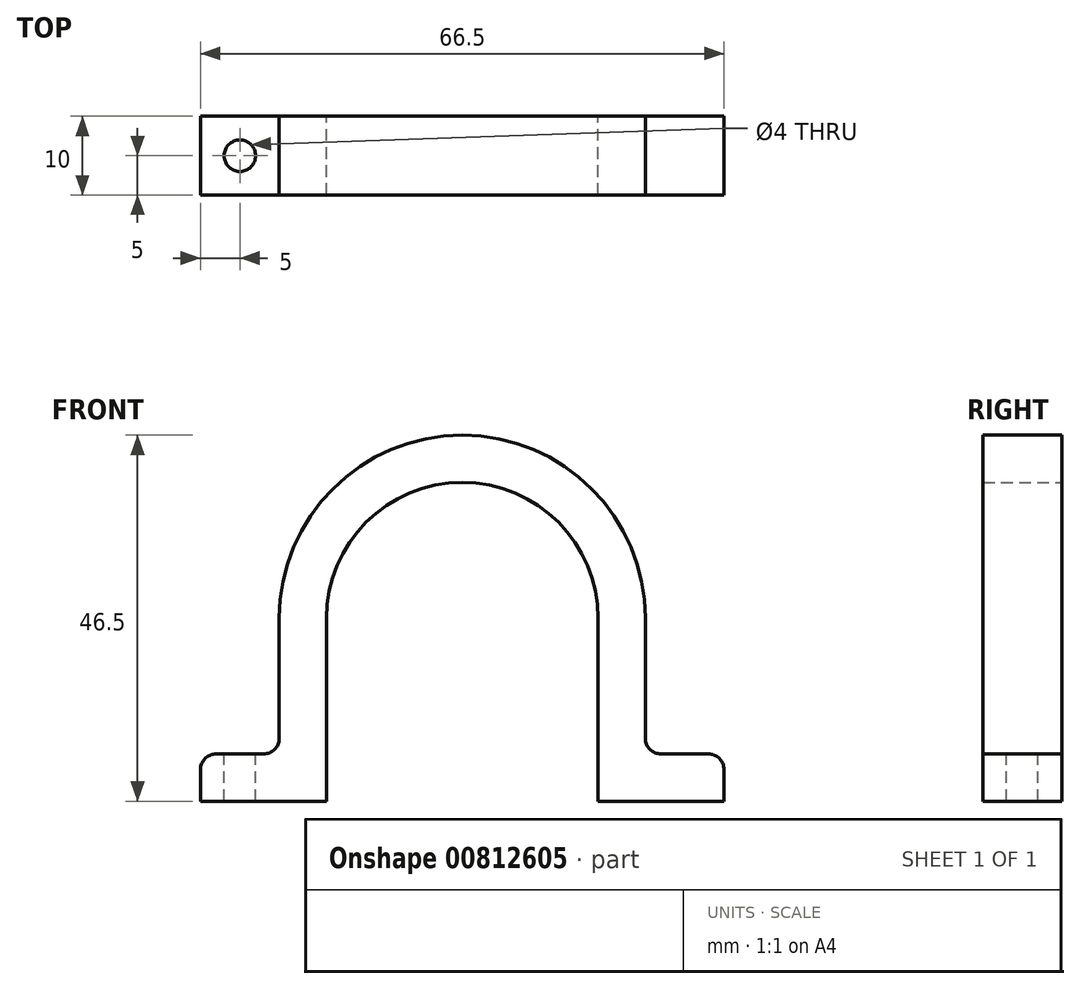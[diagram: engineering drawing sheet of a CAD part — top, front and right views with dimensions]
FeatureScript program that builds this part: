
annotation { "Feature Type Name" : "Feature", "Feature Type Description" : "" }
export const myFeature = defineFeature(function(context is Context, id is Id, definition is map)
    precondition{}
    {
        {
            var Q0;
            Q0=qCreatedBy(makeId("Front.planeOp"),FACE);
            var sketch = newSketch(context, id + "F0", { "sketchPlane" : qUnion([Q0])});
            skArc(sketch, "E0", {"start": v(17.25, 0) * mm, "mid": v(0, 17.25) * mm, "end": v(-17.25, 0) * mm});
            skArc(sketch, "E1", {"start": v(23.25, 0) * mm, "mid": v(0, 23.25) * mm, "end": v(-23.25, 0) * mm});
            skLineSegment(sketch, "E2", {"start": v(0, -23.25) * mm, "end": v(40.53, -23.25) * mm, "construction": true});
            skLineSegment(sketch, "E3", {"start": v(0, -23.25) * mm, "end": v(-44.41, -23.25) * mm, "construction": true});
            skLineSegment(sketch, "E4", {"start": v(-23.25, 0) * mm, "end": v(-23.25, -23.25) * mm});
            skLineSegment(sketch, "E5", {"start": v(-17.25, 0) * mm, "end": v(-17.25, -23.25) * mm});
            skLineSegment(sketch, "E6", {"start": v(-17.25, -23.25) * mm, "end": v(-23.25, -23.25) * mm});
            skLineSegment(sketch, "E7", {"start": v(23.25, 0) * mm, "end": v(23.25, -23.25) * mm});
            skLineSegment(sketch, "E8", {"start": v(17.25, 0) * mm, "end": v(17.25, -23.25) * mm});
            skLineSegment(sketch, "E9", {"start": v(17.25, -23.25) * mm, "end": v(23.25, -23.25) * mm});
            skLineSegment(sketch, "E10.bottom", {"start": v(-23.25, -23.25) * mm, "end": v(-33.25, -23.25) * mm});
            skLineSegment(sketch, "E10.top", {"start": v(-23.25, -17.25) * mm, "end": v(-33.25, -17.25) * mm});
            skLineSegment(sketch, "E10.left", {"start": v(-23.25, -23.25) * mm, "end": v(-23.25, -17.25) * mm});
            skLineSegment(sketch, "E10.right", {"start": v(-33.25, -23.25) * mm, "end": v(-33.25, -17.25) * mm});
            skLineSegment(sketch, "E11.bottom", {"start": v(23.25, -23.25) * mm, "end": v(33.25, -23.25) * mm});
            skLineSegment(sketch, "E11.top", {"start": v(23.25, -17.25) * mm, "end": v(33.25, -17.25) * mm});
            skLineSegment(sketch, "E11.left", {"start": v(23.25, -23.25) * mm, "end": v(23.25, -17.25) * mm});
            skLineSegment(sketch, "E11.right", {"start": v(33.25, -23.25) * mm, "end": v(33.25, -17.25) * mm});
            skSolve(sketch);
        }
        {
            var Q0;
            {var subQ0=sQuery(id+"F0.wireOp",EDGE,"E10.bottom");var subQ10=sQuery(id+"F0.wireOp",EDGE,"E11.bottom");Q0=qUnion([makeQuery(id+"F0.imprint","IMPRINT",FACE,{"disambiguationData":[TD([[makeQuery(id+"F0.imprint","IMPRINT",EDGE,{"derivedFrom":subQ0}),-1.0]])]}),makeQuery(id+"F0.imprint","IMPRINT",FACE,{"disambiguationData":[TD([[makeQuery(id+"F0.imprint","IMPRINT",EDGE,{"derivedFrom":subQ10}),1.0]])]}),makeQuery(id+"F0.imprint","IMPRINT",FACE,{"disambiguationData":[TD([[makeQuery(id+"F0.imprint","IMPRINT",EDGE,{"derivedFrom":sQuery(id+"F0.wireOp",EDGE,"E0")}),-1.0]])]})]);}
            extrude(context, id + "F1", {"entities" : qUnion([Q0]), "depth" : 10 * mm, "offsetDistance" : 25 * mm});
        }
        {
            var Q0;
            Q0=makeQuery(id+"F1.opExtrude","SWEPT_FACE",FACE,{"disambiguationData":[OSD([sQuery(id+"F0.wireOp",EDGE,"E10.top")])]});
            var sketch = newSketch(context, id + "F2", { "sketchPlane" : qUnion([Q0])});
            skLineSegment(sketch, "E12", {"start": v(-28.25, 0) * mm, "end": v(-28.25, -12.52) * mm, "construction": true});
            skLineSegment(sketch, "E13", {"start": v(-33.25, -5) * mm, "end": v(-22.13, -5) * mm, "construction": true});
            skCircle(sketch, "E14", {"center": v(-28.25, -5) * mm, "radius": 2 * mm});
            skCircle(sketch, "E15.MirrorC", {"center": v(28.25, -5) * mm, "radius": 2 * mm});
            skSolve(sketch);
        }
        {
            var Q0;
            Q0=makeQuery(id+"F2.imprint","IMPRINT",FACE,{"disambiguationData":[TD([[makeQuery(id+"F2.imprint","IMPRINT",EDGE,{"derivedFrom":sQuery(id+"F2.wireOp",EDGE,"E14")}),1.0]])]});
            var Q1;
            Q1=makeQuery(id+"F2.imprint","IMPRINT",FACE,{"disambiguationData":[TD([[makeQuery(id+"F2.imprint","IMPRINT",EDGE,{"derivedFrom":sQuery(id+"F2.wireOp",EDGE,"E15.MirrorC")}),-1.0]])]});
            var Q2;
            Q2=makeQuery(id+"F1.opExtrude","SWEPT_FACE",FACE,{"disambiguationData":[OSD([sQuery(id+"F0.wireOp",EDGE,"E6"),sQuery(id+"F0.wireOp",EDGE,"E10.bottom")])]});
            extrude(context, id + "F3", {"entities" : qUnion([Q0, Q1]), "operationType" : NewBodyOperationType.REMOVE, "endBound" : BoundingType.UP_TO_SURFACE, "oppositeDirection" : true, "depth" : 25 * mm, "endBoundEntityFace" : qUnion([Q2]), "offsetDistance" : 25 * mm});
        }
        {
            var Q0;
            Q0=makeQuery(id+"F1.opExtrude","SWEPT_EDGE",EDGE,{"disambiguationData":[OSD([sQuery(id+"F0.wireOp",EDGE,"E4"),sQuery(id+"F0.wireOp",EDGE,"E10.top")])]});
            var Q1;
            Q1=makeQuery(id+"F1.opExtrude","SWEPT_EDGE",EDGE,{"disambiguationData":[OSD([sQuery(id+"F0.wireOp",EDGE,"E7"),sQuery(id+"F0.wireOp",EDGE,"E11.top")])]});
            var Q2;
            Q2=makeQuery(id+"F1.opExtrude","SWEPT_EDGE",EDGE,{"disambiguationData":[OSD([sQuery(id+"F0.wireOp",EDGE,"E11.top"),sQuery(id+"F0.wireOp",EDGE,"E11.right")])]});
            var Q3;
            Q3=makeQuery(id+"F1.opExtrude","SWEPT_EDGE",EDGE,{"disambiguationData":[OSD([sQuery(id+"F0.wireOp",EDGE,"E10.top"),sQuery(id+"F0.wireOp",EDGE,"E10.right")])]});
            fillet(context, id + "F4", {"entities" : qUnion([Q0, Q1, Q2, Q3]), "radius" : 2 * mm, "tangentPropagation" : true, "allowEdgeOverflow" : false});
        }
    });
